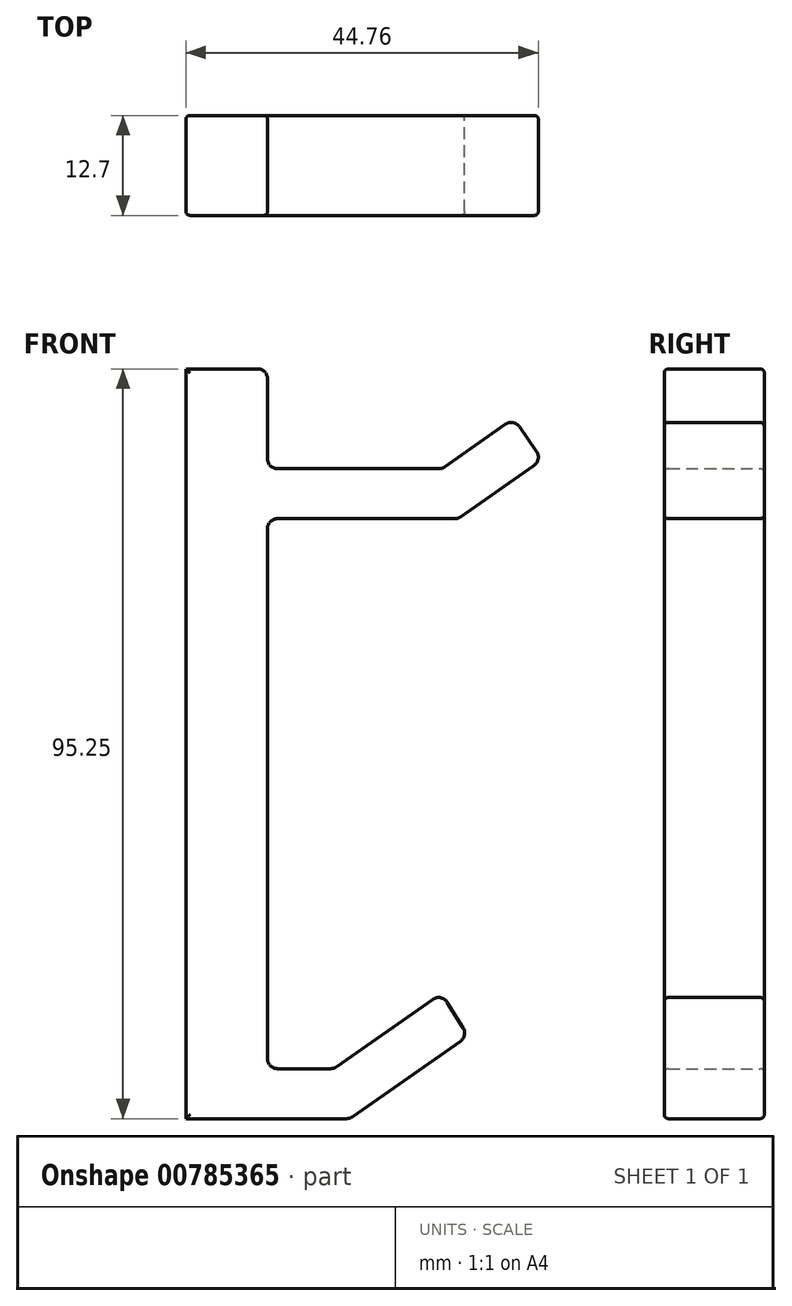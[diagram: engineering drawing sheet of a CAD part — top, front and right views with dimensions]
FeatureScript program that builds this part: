
annotation { "Feature Type Name" : "Feature", "Feature Type Description" : "" }
export const myFeature = defineFeature(function(context is Context, id is Id, definition is map)
    precondition{}
    {
        {
            var Q0;
            Q0=qCreatedBy(makeId("Front.planeOp"),FACE);
            var sketch = newSketch(context, id + "F0", { "sketchPlane" : qUnion([Q0])});
            skLineSegment(sketch, "E0", {"start": v(-33.7, 50.02) * mm, "end": v(-33.7, -38.88) * mm});
            skLineSegment(sketch, "E1", {"start": v(-23.32, 48.75) * mm, "end": v(-23.32, 38.6) * mm});
            skLineSegment(sketch, "E2", {"start": v(-24.6, 50.02) * mm, "end": v(-33.7, 50.02) * mm});
            skLineSegment(sketch, "E3", {"start": v(-22.05, 37.33) * mm, "end": v(-1.57, 37.33) * mm});
            skLineSegment(sketch, "E4", {"start": v(-0.84, 37.56) * mm, "end": v(6.9, 42.98) * mm});
            skLineSegment(sketch, "E5", {"start": v(-22.05, -38.88) * mm, "end": v(-15.29, -38.88) * mm});
            skLineSegment(sketch, "E6", {"start": v(-14.56, -38.65) * mm, "end": v(-2.3, -30.07) * mm});
            skLineSegment(sketch, "E7.0", {"start": v(1.17, 31.21) * mm, "end": v(10.53, 37.77) * mm});
            skLineSegment(sketch, "E7.1", {"start": v(-22.05, 30.98) * mm, "end": v(0.44, 30.98) * mm});
            skLineSegment(sketch, "E8.0", {"start": v(-12.56, -45) * mm, "end": v(1.17, -35.4) * mm});
            skLineSegment(sketch, "E8.1", {"start": v(-23.32, -45.23) * mm, "end": v(-13.29, -45.23) * mm});
            skLineSegment(sketch, "E9", {"start": v(-0.5, -30.44) * mm, "end": v(1.51, -33.68) * mm});
            skLineSegment(sketch, "E10", {"start": v(8.68, 42.67) * mm, "end": v(10.85, 39.53) * mm});
            skLineSegment(sketch, "E11", {"start": v(-23.32, -45.23) * mm, "end": v(-33.7, -45.23) * mm});
            skLineSegment(sketch, "E12", {"start": v(-33.7, -45.23) * mm, "end": v(-33.7, -38.88) * mm});
            skLineSegment(sketch, "E13.trimOffspring", {"start": v(-23.32, 29.71) * mm, "end": v(-23.32, -37.6) * mm});
            skPoint(sketch, "E14.visualSharp", {"position": v(7.95, 43.72) * mm});
            skArc(sketch, "E14.filletArc", {"start": v(8.68, 42.67) * mm, "mid": v(7.86, 43.2) * mm, "end": v(6.9, 42.98) * mm});
            skPoint(sketch, "E15.visualSharp", {"position": v(-1.21, -29.3) * mm});
            skArc(sketch, "E15.filletArc", {"start": v(-0.5, -30.44) * mm, "mid": v(-1.33, -29.87) * mm, "end": v(-2.3, -30.07) * mm});
            skPoint(sketch, "E16.visualSharp", {"position": v(2.15, -34.7) * mm});
            skArc(sketch, "E16.filletArc", {"start": v(1.17, -35.4) * mm, "mid": v(1.68, -34.6) * mm, "end": v(1.51, -33.68) * mm});
            skPoint(sketch, "E17.visualSharp", {"position": v(11.57, 38.5) * mm});
            skArc(sketch, "E17.filletArc", {"start": v(10.53, 37.77) * mm, "mid": v(11.05, 38.59) * mm, "end": v(10.85, 39.53) * mm});
            skPoint(sketch, "E18.visualSharp", {"position": v(-23.32, 50.02) * mm});
            skArc(sketch, "E18.filletArc", {"start": v(-23.32, 48.75) * mm, "mid": v(-23.7, 49.65) * mm, "end": v(-24.6, 50.02) * mm});
            skPoint(sketch, "E19.visualSharp", {"position": v(-1.17, 37.33) * mm});
            skArc(sketch, "E19.filletArc", {"start": v(-1.57, 37.33) * mm, "mid": v(-1.18, 37.4) * mm, "end": v(-0.84, 37.56) * mm});
            skPoint(sketch, "E20.visualSharp", {"position": v(0.84, 30.98) * mm});
            skArc(sketch, "E20.filletArc", {"start": v(0.44, 30.98) * mm, "mid": v(0.82, 31.04) * mm, "end": v(1.17, 31.21) * mm});
            skPoint(sketch, "E21.visualSharp", {"position": v(-14.89, -38.88) * mm});
            skArc(sketch, "E21.filletArc", {"start": v(-15.29, -38.88) * mm, "mid": v(-14.9, -38.82) * mm, "end": v(-14.56, -38.65) * mm});
            skPoint(sketch, "E22.visualSharp", {"position": v(-12.89, -45.23) * mm});
            skArc(sketch, "E22.filletArc", {"start": v(-13.29, -45.23) * mm, "mid": v(-12.9, -45.17) * mm, "end": v(-12.56, -45) * mm});
            skPoint(sketch, "E23.visualSharp", {"position": v(-23.32, 37.33) * mm});
            skArc(sketch, "E23.filletArc", {"start": v(-23.32, 38.6) * mm, "mid": v(-22.95, 37.7) * mm, "end": v(-22.05, 37.33) * mm});
            skPoint(sketch, "E24.visualSharp", {"position": v(-23.32, 30.98) * mm});
            skArc(sketch, "E24.filletArc", {"start": v(-22.05, 30.98) * mm, "mid": v(-22.95, 30.61) * mm, "end": v(-23.32, 29.71) * mm});
            skPoint(sketch, "E25.visualSharp", {"position": v(-23.32, -38.88) * mm});
            skArc(sketch, "E25.filletArc", {"start": v(-23.32, -37.6) * mm, "mid": v(-22.95, -38.5) * mm, "end": v(-22.05, -38.88) * mm});
            skSolve(sketch);
        }
        {
            var Q0;
            {var subQ0=sQuery(id+"F0.wireOp",EDGE,"E3");Q0=makeQuery(id+"F0.imprint","IMPRINT",FACE,{"disambiguationData":[TD([[makeQuery(id+"F0.imprint","IMPRINT",EDGE,{"derivedFrom":subQ0}),-1.0]])]});}
            var Q1;
            Q1=makeQuery(id+"F0.imprint","IMPRINT",FACE,{"disambiguationData":[TD([[makeQuery(id+"F0.imprint","IMPRINT",EDGE,{"derivedFrom":sQuery(id+"F0.wireOp",EDGE,"E0")}),1.0]])]});
            extrude(context, id + "F1", {"entities" : qUnion([Q0, Q1]), "depth" : 12.7 * mm, "offsetDistance" : 25.4 * mm});
        }
        {
            var Q0;
            Q0=makeQuery(id+"F1.opExtrude","CAP_FACE",FACE,{"disambiguationData":[OSD([sQuery(id+"F0.wireOp",EDGE,"E0"),sQuery(id+"F0.wireOp",EDGE,"E1"),sQuery(id+"F0.wireOp",EDGE,"E2"),sQuery(id+"F0.wireOp",EDGE,"E3"),sQuery(id+"F0.wireOp",EDGE,"E4"),sQuery(id+"F0.wireOp",EDGE,"E5"),sQuery(id+"F0.wireOp",EDGE,"E6"),sQuery(id+"F0.wireOp",EDGE,"E7.0"),sQuery(id+"F0.wireOp",EDGE,"E7.1"),sQuery(id+"F0.wireOp",EDGE,"E8.0"),sQuery(id+"F0.wireOp",EDGE,"E8.1"),sQuery(id+"F0.wireOp",EDGE,"E9"),sQuery(id+"F0.wireOp",EDGE,"E10"),sQuery(id+"F0.wireOp",EDGE,"E11"),sQuery(id+"F0.wireOp",EDGE,"E12"),sQuery(id+"F0.wireOp",EDGE,"E13.trimOffspring"),sQuery(id+"F0.wireOp",EDGE,"E14.filletArc"),sQuery(id+"F0.wireOp",EDGE,"E15.filletArc"),sQuery(id+"F0.wireOp",EDGE,"E16.filletArc"),sQuery(id+"F0.wireOp",EDGE,"E17.filletArc"),sQuery(id+"F0.wireOp",EDGE,"E18.filletArc"),sQuery(id+"F0.wireOp",EDGE,"E19.filletArc"),sQuery(id+"F0.wireOp",EDGE,"E20.filletArc"),sQuery(id+"F0.wireOp",EDGE,"E21.filletArc"),sQuery(id+"F0.wireOp",EDGE,"E22.filletArc")])],"isStart":false});
            var Q1;
            Q1=makeQuery(id+"F1.opExtrude","CAP_FACE",FACE,{"disambiguationData":[OSD([sQuery(id+"F0.wireOp",EDGE,"E0"),sQuery(id+"F0.wireOp",EDGE,"E1"),sQuery(id+"F0.wireOp",EDGE,"E2"),sQuery(id+"F0.wireOp",EDGE,"E3"),sQuery(id+"F0.wireOp",EDGE,"E4"),sQuery(id+"F0.wireOp",EDGE,"E5"),sQuery(id+"F0.wireOp",EDGE,"E6"),sQuery(id+"F0.wireOp",EDGE,"E7.0"),sQuery(id+"F0.wireOp",EDGE,"E7.1"),sQuery(id+"F0.wireOp",EDGE,"E8.0"),sQuery(id+"F0.wireOp",EDGE,"E8.1"),sQuery(id+"F0.wireOp",EDGE,"E9"),sQuery(id+"F0.wireOp",EDGE,"E10"),sQuery(id+"F0.wireOp",EDGE,"E11"),sQuery(id+"F0.wireOp",EDGE,"E12"),sQuery(id+"F0.wireOp",EDGE,"E13.trimOffspring"),sQuery(id+"F0.wireOp",EDGE,"E14.filletArc"),sQuery(id+"F0.wireOp",EDGE,"E15.filletArc"),sQuery(id+"F0.wireOp",EDGE,"E16.filletArc"),sQuery(id+"F0.wireOp",EDGE,"E17.filletArc"),sQuery(id+"F0.wireOp",EDGE,"E18.filletArc"),sQuery(id+"F0.wireOp",EDGE,"E19.filletArc"),sQuery(id+"F0.wireOp",EDGE,"E20.filletArc"),sQuery(id+"F0.wireOp",EDGE,"E21.filletArc"),sQuery(id+"F0.wireOp",EDGE,"E22.filletArc")])],"isStart":true});
            fillet(context, id + "F2", {"entities" : qUnion([Q0, Q1]), "radius" : 0.5 * mm, "tangentPropagation" : true, "allowEdgeOverflow" : false});
        }
    });
